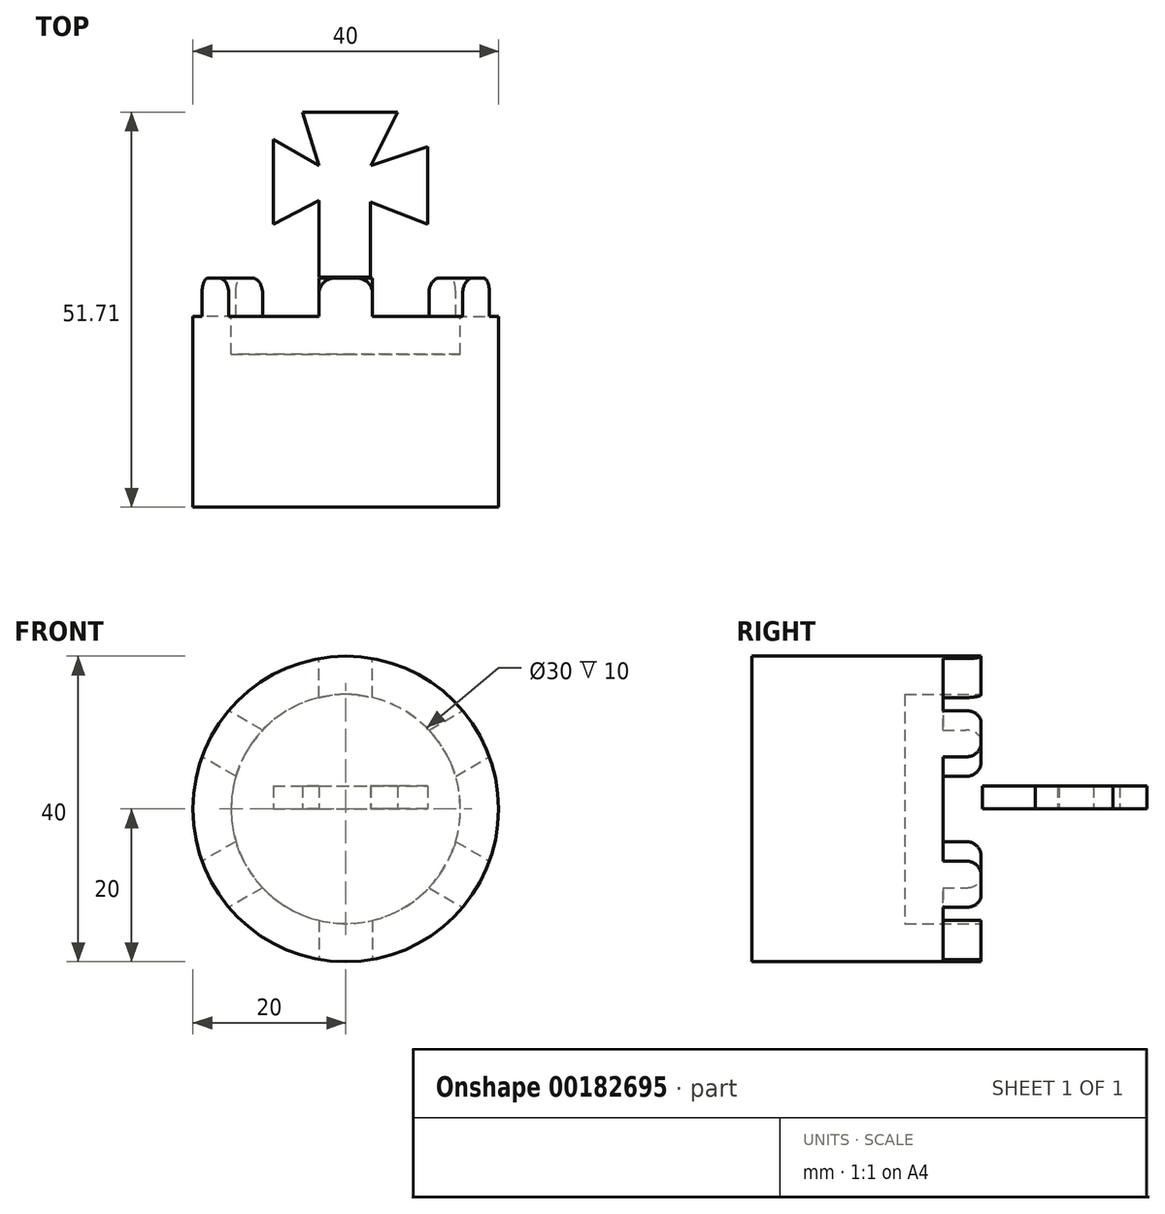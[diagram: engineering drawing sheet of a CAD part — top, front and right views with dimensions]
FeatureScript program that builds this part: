
annotation { "Feature Type Name" : "Feature", "Feature Type Description" : "" }
export const myFeature = defineFeature(function(context is Context, id is Id, definition is map)
    precondition{}
    {
        {
            var Q0;
            Q0=qCreatedBy(makeId("Front.planeOp"),FACE);
            var sketch = newSketch(context, id + "F0", { "sketchPlane" : qUnion([Q0])});
            skCircle(sketch, "E0", {"center": v(0, 0) * mm, "radius": 20 * mm});
            skSolve(sketch);
        }
        {
            var Q0;
            Q0=makeQuery(id+"F0.imprint","IMPRINT",FACE,{"disambiguationData":[TD([[makeQuery(id+"F0.imprint","IMPRINT",EDGE,{"derivedFrom":sQuery(id+"F0.wireOp",EDGE,"E0")}),1.0]])]});
            var Q1;
            Q1 = qSketchRegion(id + "F2", true);
            extrude(context, id + "F1", {"entities" : qUnion([Q0, Q1]), "oppositeDirection" : true, "depth" : 30 * mm});
        }
        {
            var Q0;
            Q0=makeQuery(id+"F1.opExtrude","CAP_FACE",FACE,{"disambiguationData":[OSD([sQuery(id+"F0.wireOp",EDGE,"E0")])],"isStart":false});
            var sketch = newSketch(context, id + "F2", { "sketchPlane" : qUnion([Q0])});
            skCircle(sketch, "E1", {"center": v(0, 0) * mm, "radius": 15 * mm});
            skSolve(sketch);
        }
        {
            var Q0;
            Q0=qSketchRegion(id+"F2",true);
            extrude(context, id + "F3", {"entities" : qUnion([Q0]), "operationType" : NewBodyOperationType.REMOVE, "oppositeDirection" : true, "depth" : 10 * mm});
        }
        {
            var Q0;
            Q0=makeQuery(id+"F1.opExtrude","CAP_FACE",FACE,{"disambiguationData":[OSD([sQuery(id+"F0.wireOp",EDGE,"E0")])],"isStart":false});
            var sketch = newSketch(context, id + "F4", { "sketchPlane" : qUnion([Q0])});
            skLineSegment(sketch, "E2.bottom", {"start": v(-3.5, -14.59) * mm, "end": v(3.5, -14.59) * mm});
            skLineSegment(sketch, "E2.top", {"start": v(-3.5, -19.7) * mm, "end": v(3.5, -19.7) * mm, "construction": true});
            skLineSegment(sketch, "E2.left", {"start": v(-3.5, -14.59) * mm, "end": v(-3.5, -19.7) * mm});
            skLineSegment(sketch, "E2.right", {"start": v(3.5, -14.59) * mm, "end": v(3.5, -19.7) * mm});
            skLineSegment(sketch, "E3", {"start": v(0, -19.7) * mm, "end": v(0, 0) * mm, "construction": true});
            skArc(sketch, "E4", {"start": v(-3.5, -19.7) * mm, "mid": v(0, -20) * mm, "end": v(3.5, -19.7) * mm});
            skLineSegment(sketch, "E5.1.0", {"start": v(10.88, -10.32) * mm, "end": v(15.3, -12.88) * mm});
            skLineSegment(sketch, "E5.1.1", {"start": v(10.88, -10.32) * mm, "end": v(14.38, -4.26) * mm});
            skLineSegment(sketch, "E5.1.2", {"start": v(15.3, -12.88) * mm, "end": v(18.8, -6.81) * mm, "construction": true});
            skLineSegment(sketch, "E5.1.3", {"start": v(14.38, -4.26) * mm, "end": v(18.8, -6.81) * mm});
            skArc(sketch, "E5.1.4", {"start": v(15.3, -12.88) * mm, "mid": v(17.32, -10) * mm, "end": v(18.8, -6.81) * mm});
            skLineSegment(sketch, "E5.2.0", {"start": v(14.38, 4.26) * mm, "end": v(18.8, 6.81) * mm});
            skLineSegment(sketch, "E5.2.1", {"start": v(14.38, 4.26) * mm, "end": v(10.88, 10.32) * mm});
            skLineSegment(sketch, "E5.2.2", {"start": v(18.8, 6.81) * mm, "end": v(15.3, 12.88) * mm, "construction": true});
            skLineSegment(sketch, "E5.2.3", {"start": v(10.88, 10.32) * mm, "end": v(15.3, 12.88) * mm});
            skArc(sketch, "E5.2.4", {"start": v(18.8, 6.81) * mm, "mid": v(17.32, 10) * mm, "end": v(15.3, 12.88) * mm});
            skLineSegment(sketch, "E5.3.0", {"start": v(3.5, 14.59) * mm, "end": v(3.5, 19.7) * mm});
            skLineSegment(sketch, "E5.3.1", {"start": v(3.5, 14.59) * mm, "end": v(-3.5, 14.59) * mm});
            skLineSegment(sketch, "E5.3.2", {"start": v(3.5, 19.7) * mm, "end": v(-3.5, 19.7) * mm, "construction": true});
            skLineSegment(sketch, "E5.3.3", {"start": v(-3.5, 14.59) * mm, "end": v(-3.5, 19.7) * mm});
            skArc(sketch, "E5.3.4", {"start": v(3.5, 19.7) * mm, "mid": v(0, 20) * mm, "end": v(-3.5, 19.7) * mm});
            skLineSegment(sketch, "E5.4.0", {"start": v(-10.88, 10.32) * mm, "end": v(-15.3, 12.88) * mm});
            skLineSegment(sketch, "E5.4.1", {"start": v(-10.88, 10.32) * mm, "end": v(-14.38, 4.26) * mm});
            skLineSegment(sketch, "E5.4.2", {"start": v(-15.3, 12.88) * mm, "end": v(-18.8, 6.81) * mm, "construction": true});
            skLineSegment(sketch, "E5.4.3", {"start": v(-14.38, 4.26) * mm, "end": v(-18.8, 6.81) * mm});
            skArc(sketch, "E5.4.4", {"start": v(-15.3, 12.88) * mm, "mid": v(-17.32, 10) * mm, "end": v(-18.8, 6.81) * mm});
            skLineSegment(sketch, "E5.5.0", {"start": v(-14.38, -4.26) * mm, "end": v(-18.8, -6.81) * mm});
            skLineSegment(sketch, "E5.5.1", {"start": v(-14.38, -4.26) * mm, "end": v(-10.88, -10.32) * mm});
            skLineSegment(sketch, "E5.5.2", {"start": v(-18.8, -6.81) * mm, "end": v(-15.3, -12.88) * mm, "construction": true});
            skLineSegment(sketch, "E5.5.3", {"start": v(-10.88, -10.32) * mm, "end": v(-15.3, -12.88) * mm});
            skArc(sketch, "E5.5.4", {"start": v(-18.8, -6.81) * mm, "mid": v(-17.32, -10) * mm, "end": v(-15.3, -12.88) * mm});
            skSolve(sketch);
        }
        {
            var Q0;
            {var subQ0=sQuery(id+"F4.wireOp",EDGE,"E2.left");var subQ3=makeQuery(id+"F1.opExtrude","CAP_EDGE",EDGE,{"disambiguationData":[OSD([sQuery(id+"F0.wireOp",EDGE,"E0")])],"isStart":false});var subQ4=makeQuery(id+"F4.imprint","INTERSECT",VERTEX,{"derivedFrom":[subQ3,subQ0]});Q0=makeQuery(id+"F4.imprint","IMPRINT",FACE,{"disambiguationData":[TD([[makeQuery(id+"F4.imprint","IMPRINT",EDGE,{"disambiguationData":[TD([[subQ4,1.0]])],"derivedFrom":subQ0}),-1.0]])]});}
            var Q1;
            {var subQ0=sQuery(id+"F4.wireOp",EDGE,"E5.4.3");Q1=makeQuery(id+"F4.imprint","IMPRINT",FACE,{"disambiguationData":[TD([[makeQuery(id+"F4.imprint","IMPRINT",EDGE,{"derivedFrom":subQ0}),1.0]])]});}
            var Q2;
            {var subQ0=sQuery(id+"F4.wireOp",EDGE,"E5.3.3");Q2=makeQuery(id+"F4.imprint","IMPRINT",FACE,{"disambiguationData":[TD([[makeQuery(id+"F4.imprint","IMPRINT",EDGE,{"derivedFrom":subQ0}),1.0]])]});}
            var Q3;
            {var subQ0=sQuery(id+"F4.wireOp",EDGE,"E5.2.3");Q3=makeQuery(id+"F4.imprint","IMPRINT",FACE,{"disambiguationData":[TD([[makeQuery(id+"F4.imprint","IMPRINT",EDGE,{"derivedFrom":subQ0}),1.0]])]});}
            var Q4;
            {var subQ0=sQuery(id+"F4.wireOp",EDGE,"E5.1.3");Q4=makeQuery(id+"F4.imprint","IMPRINT",FACE,{"disambiguationData":[TD([[makeQuery(id+"F4.imprint","IMPRINT",EDGE,{"derivedFrom":subQ0}),1.0]])]});}
            var Q5;
            {var subQ0=sQuery(id+"F4.wireOp",EDGE,"E2.right");Q5=makeQuery(id+"F4.imprint","IMPRINT",FACE,{"disambiguationData":[TD([[makeQuery(id+"F4.imprint","IMPRINT",EDGE,{"derivedFrom":subQ0}),1.0]])]});}
            extrude(context, id + "F5", {"entities" : qUnion([Q0, Q1, Q2, Q3, Q4, Q5]), "operationType" : NewBodyOperationType.REMOVE, "oppositeDirection" : true, "depth" : 5 * mm});
        }
        {
            var Q0;
            Q0=makeQuery(id+"F5.boolean.opBoolean","COPY",EDGE,{"derivedFrom":makeQuery(id+"F5.opExtrude","CAP_EDGE",EDGE,{"disambiguationData":[OSD([sQuery(id+"F4.wireOp",EDGE,"E2.right")])],"isStart":true})});
            var Q1;
            Q1=makeQuery(id+"F5.boolean.opBoolean","COPY",EDGE,{"derivedFrom":makeQuery(id+"F5.opExtrude","CAP_EDGE",EDGE,{"disambiguationData":[OSD([sQuery(id+"F4.wireOp",EDGE,"E2.left")])],"isStart":true})});
            var Q2;
            Q2=makeQuery(id+"F5.boolean.opBoolean","COPY",EDGE,{"derivedFrom":makeQuery(id+"F5.opExtrude","CAP_EDGE",EDGE,{"disambiguationData":[OSD([sQuery(id+"F4.wireOp",EDGE,"E5.5.3")])],"isStart":true})});
            var Q3;
            Q3=makeQuery(id+"F5.boolean.opBoolean","COPY",EDGE,{"derivedFrom":makeQuery(id+"F5.opExtrude","CAP_EDGE",EDGE,{"disambiguationData":[OSD([sQuery(id+"F4.wireOp",EDGE,"E5.5.0")])],"isStart":true})});
            var Q4;
            Q4=makeQuery(id+"F5.boolean.opBoolean","COPY",EDGE,{"derivedFrom":makeQuery(id+"F5.opExtrude","CAP_EDGE",EDGE,{"disambiguationData":[OSD([sQuery(id+"F4.wireOp",EDGE,"E5.4.3")])],"isStart":true})});
            var Q5;
            Q5=makeQuery(id+"F5.boolean.opBoolean","COPY",EDGE,{"derivedFrom":makeQuery(id+"F5.opExtrude","CAP_EDGE",EDGE,{"disambiguationData":[OSD([sQuery(id+"F4.wireOp",EDGE,"E5.3.3")])],"isStart":true})});
            var Q6;
            Q6=makeQuery(id+"F5.boolean.opBoolean","COPY",EDGE,{"derivedFrom":makeQuery(id+"F5.opExtrude","CAP_EDGE",EDGE,{"disambiguationData":[OSD([sQuery(id+"F4.wireOp",EDGE,"E5.3.0")])],"isStart":true})});
            var Q7;
            Q7=makeQuery(id+"F5.boolean.opBoolean","COPY",EDGE,{"derivedFrom":makeQuery(id+"F5.opExtrude","CAP_EDGE",EDGE,{"disambiguationData":[OSD([sQuery(id+"F4.wireOp",EDGE,"E5.2.3")])],"isStart":true})});
            var Q8;
            Q8=makeQuery(id+"F5.boolean.opBoolean","COPY",EDGE,{"derivedFrom":makeQuery(id+"F5.opExtrude","CAP_EDGE",EDGE,{"disambiguationData":[OSD([sQuery(id+"F4.wireOp",EDGE,"E5.2.0")])],"isStart":true})});
            var Q9;
            Q9=makeQuery(id+"F5.boolean.opBoolean","COPY",EDGE,{"derivedFrom":makeQuery(id+"F5.opExtrude","CAP_EDGE",EDGE,{"disambiguationData":[OSD([sQuery(id+"F4.wireOp",EDGE,"E5.1.3")])],"isStart":true})});
            var Q10;
            Q10=makeQuery(id+"F5.boolean.opBoolean","COPY",EDGE,{"derivedFrom":makeQuery(id+"F5.opExtrude","CAP_EDGE",EDGE,{"disambiguationData":[OSD([sQuery(id+"F4.wireOp",EDGE,"E5.1.0")])],"isStart":true})});
            var Q11;
            Q11=makeQuery(id+"F5.boolean.opBoolean","COPY",EDGE,{"derivedFrom":makeQuery(id+"F5.opExtrude","CAP_EDGE",EDGE,{"disambiguationData":[OSD([sQuery(id+"F4.wireOp",EDGE,"E5.4.0")])],"isStart":true})});
            fillet(context, id + "F6", {"entities" : qUnion([Q0, Q1, Q2, Q3, Q4, Q5, Q6, Q7, Q8, Q9, Q10, Q11]), "radius" : 2 * mm, "tangentPropagation" : true, "allowEdgeOverflow" : false});
        }
        {
            var Q0;
            Q0=qCreatedBy(makeId("Top.planeOp"),FACE);
            var sketch = newSketch(context, id + "F7", { "sketchPlane" : qUnion([Q0])});
            skLineSegment(sketch, "E6", {"start": v(-3.51, 30.13) * mm, "end": v(-3.51, 40.17) * mm});
            skLineSegment(sketch, "E7", {"start": v(-3.51, 40.17) * mm, "end": v(-9.47, 37.06) * mm});
            skLineSegment(sketch, "E8", {"start": v(-9.47, 37.06) * mm, "end": v(-9.47, 48.14) * mm});
            skLineSegment(sketch, "E9", {"start": v(-9.47, 48.14) * mm, "end": v(-3.51, 44.7) * mm});
            skLineSegment(sketch, "E10", {"start": v(-3.51, 44.7) * mm, "end": v(-5.65, 51.7) * mm});
            skLineSegment(sketch, "E11", {"start": v(-5.65, 51.7) * mm, "end": v(6.8, 51.7) * mm});
            skLineSegment(sketch, "E12", {"start": v(6.8, 51.7) * mm, "end": v(3.3, 44.7) * mm});
            skLineSegment(sketch, "E13", {"start": v(3.3, 44.7) * mm, "end": v(10.74, 47.24) * mm});
            skLineSegment(sketch, "E14", {"start": v(10.74, 47.24) * mm, "end": v(10.74, 37.06) * mm});
            skLineSegment(sketch, "E15", {"start": v(10.74, 37.06) * mm, "end": v(3.23, 39.98) * mm});
            skLineSegment(sketch, "E16", {"start": v(3.23, 39.98) * mm, "end": v(3.23, 30.2) * mm});
            skLineSegment(sketch, "E17", {"start": v(-3.51, 30.13) * mm, "end": v(3.23, 30.2) * mm});
            skSolve(sketch);
        }
        {
            var Q0;
            Q0=qSketchRegion(id+"F7",true);
            extrude(context, id + "F8", {"entities" : qUnion([Q0]), "depth" : 3 * mm});
        }
    });
